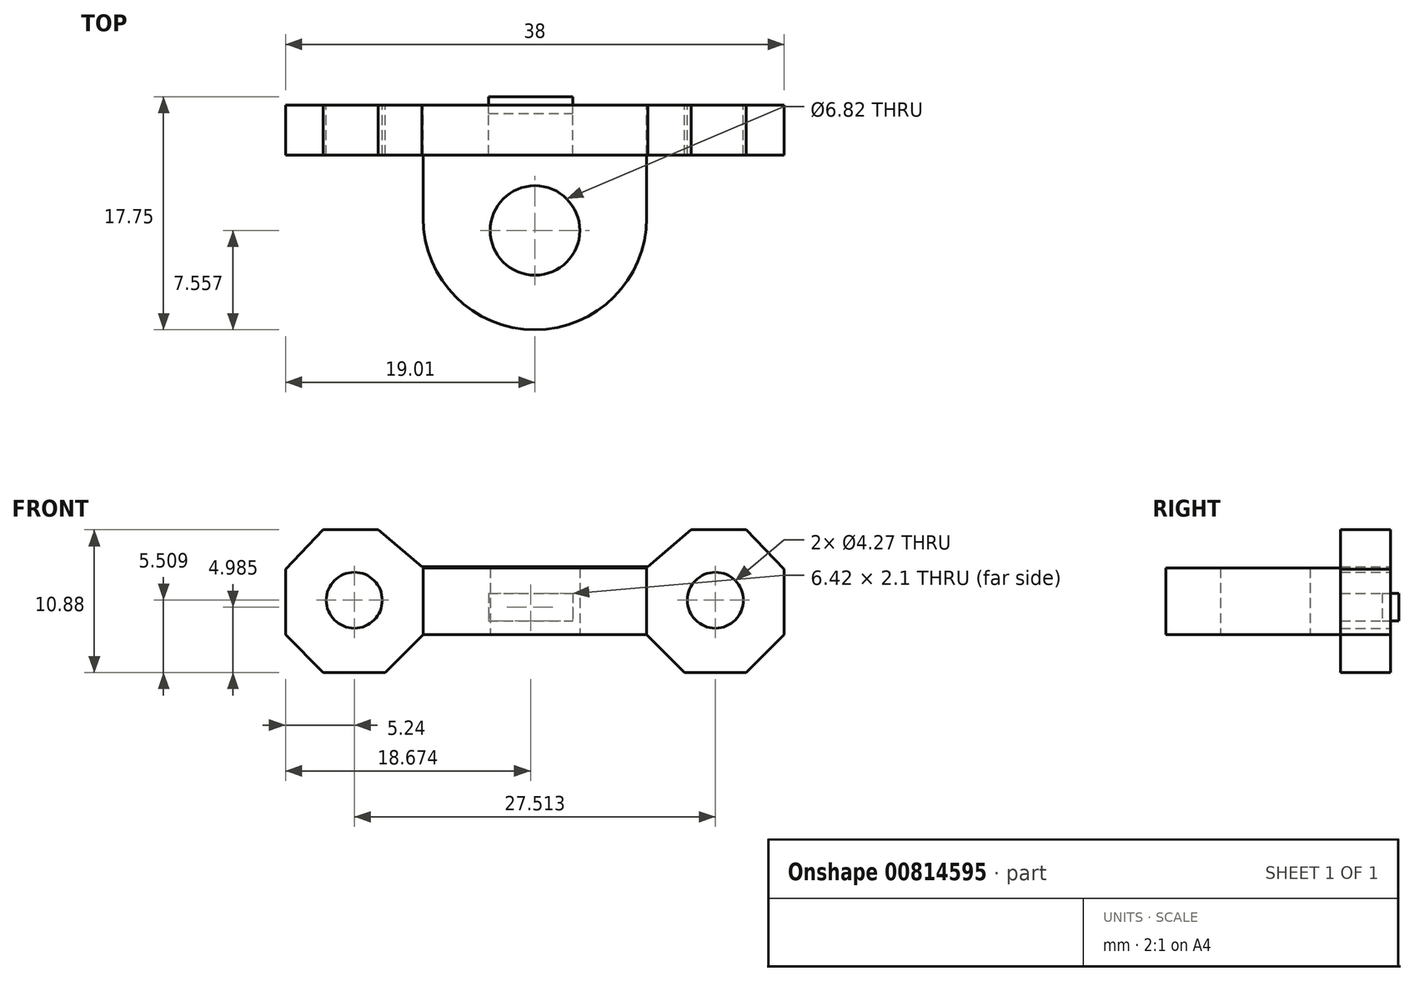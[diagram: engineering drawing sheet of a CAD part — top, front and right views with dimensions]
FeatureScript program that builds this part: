
annotation { "Feature Type Name" : "Feature", "Feature Type Description" : "" }
export const myFeature = defineFeature(function(context is Context, id is Id, definition is map)
    precondition{}
    {
        {
            var Q0;
            Q0=qCreatedBy(makeId("Front.planeOp"),FACE);
            var sketch = newSketch(context, id + "F0", { "sketchPlane" : qUnion([Q0])});
            skLineSegment(sketch, "E0", {"start": v(-50.5, 31.8) * mm, "end": v(-53.83, 34.6) * mm});
            skLineSegment(sketch, "E1", {"start": v(-53.83, 34.6) * mm, "end": v(-58.02, 34.6) * mm});
            skLineSegment(sketch, "E2", {"start": v(-58.02, 34.6) * mm, "end": v(-60.9, 31.59) * mm});
            skLineSegment(sketch, "E3", {"start": v(-60.9, 31.59) * mm, "end": v(-60.9, 26.6) * mm});
            skLineSegment(sketch, "E4", {"start": v(-60.9, 26.6) * mm, "end": v(-58.02, 23.72) * mm});
            skLineSegment(sketch, "E5", {"start": v(-58.02, 23.72) * mm, "end": v(-53.3, 23.72) * mm});
            skLineSegment(sketch, "E6", {"start": v(-53.3, 23.72) * mm, "end": v(-50.42, 26.6) * mm});
            skLineSegment(sketch, "E7", {"start": v(-50.42, 26.6) * mm, "end": v(-41.9, 26.6) * mm});
            skLineSegment(sketch, "E8", {"start": v(-50.5, 31.8) * mm, "end": v(-41.9, 31.8) * mm});
            skLineSegment(sketch, "E9", {"start": v(-41.9, 31.8) * mm, "end": v(-41.9, 26.6) * mm});
            skLineSegment(sketch, "E10.MirrorCS", {"start": v(-29.98, 34.6) * mm, "end": v(-25.79, 34.6) * mm});
            skLineSegment(sketch, "E11.MirrorCS", {"start": v(-33.3, 31.8) * mm, "end": v(-29.98, 34.6) * mm});
            skLineSegment(sketch, "E12.MirrorCS", {"start": v(-33.3, 31.8) * mm, "end": v(-41.9, 31.8) * mm});
            skLineSegment(sketch, "E13.MirrorCS", {"start": v(-33.39, 26.6) * mm, "end": v(-41.9, 26.6) * mm});
            skLineSegment(sketch, "E14.MirrorCS", {"start": v(-30.5, 23.72) * mm, "end": v(-33.39, 26.6) * mm});
            skLineSegment(sketch, "E15.MirrorCS", {"start": v(-25.79, 23.72) * mm, "end": v(-30.5, 23.72) * mm});
            skLineSegment(sketch, "E16.MirrorCS", {"start": v(-22.9, 26.6) * mm, "end": v(-25.79, 23.72) * mm});
            skLineSegment(sketch, "E17.MirrorCS", {"start": v(-22.9, 31.59) * mm, "end": v(-22.9, 26.6) * mm});
            skLineSegment(sketch, "E18.MirrorCS", {"start": v(-25.79, 34.6) * mm, "end": v(-22.9, 31.59) * mm});
            skCircle(sketch, "E19", {"center": v(-55.66, 29.23) * mm, "radius": 2.13 * mm});
            skCircle(sketch, "E20.MirrorC", {"center": v(-28.15, 29.23) * mm, "radius": 2.13 * mm});
            skLineSegment(sketch, "E21.bottom", {"start": v(-45.44, 29.75) * mm, "end": v(-39.01, 29.75) * mm});
            skLineSegment(sketch, "E21.top", {"start": v(-45.44, 27.66) * mm, "end": v(-39.01, 27.66) * mm});
            skLineSegment(sketch, "E21.left", {"start": v(-45.44, 29.75) * mm, "end": v(-45.44, 27.66) * mm});
            skLineSegment(sketch, "E21.right", {"start": v(-39.01, 29.75) * mm, "end": v(-39.01, 27.66) * mm});
            skSolve(sketch);
        }
        {
            var Q0;
            Q0 = qSketchRegion(id + "F0", true);
            extrude(context, id + "F1", {"entities" : qUnion([Q0]), "depth" : 3.8 * mm, "offsetDistance" : 25.4 * mm});
        }
        {
            var Q0;
            {var subQ5=sQuery(id+"F0.wireOp",EDGE,"E21.right");Q0=makeQuery(id+"F0.imprint","IMPRINT",FACE,{"disambiguationData":[TD([[makeQuery(id+"F0.imprint","IMPRINT",EDGE,{"derivedFrom":subQ5}),-1.0]])]});}
            var Q1;
            {var subQ5=sQuery(id+"F0.wireOp",EDGE,"E21.left");Q1=makeQuery(id+"F0.imprint","IMPRINT",FACE,{"disambiguationData":[TD([[makeQuery(id+"F0.imprint","IMPRINT",EDGE,{"derivedFrom":subQ5}),1.0]])]});}
            extrude(context, id + "F2", {"entities" : qUnion([Q0, Q1]), "endBound" : BoundingType.SYMMETRIC, "depth" : 1.27 * mm, "offsetDistance" : 25.4 * mm});
        }
        {
            var Q0;
            Q0=makeQuery(id+"F1.opExtrude","SWEPT_FACE",FACE,{"disambiguationData":[OSD([sQuery(id+"F0.wireOp",EDGE,"E7"),sQuery(id+"F0.wireOp",EDGE,"E13.MirrorCS")])]});
            var sketch = newSketch(context, id + "F3", { "sketchPlane" : qUnion([Q0])});
            skLineSegment(sketch, "E22", {"start": v(-50.42, 3.8) * mm, "end": v(-46.6, 3.81) * mm});
            skLineSegment(sketch, "E23", {"start": v(-36.63, 3.81) * mm, "end": v(-33.39, 3.81) * mm});
            skLineSegment(sketch, "E24", {"start": v(-50.42, 3.8) * mm, "end": v(-50.42, 8.6) * mm});
            skPoint(sketch, "E24.endSnap0", {"position": v(-41.61, 8.6) * mm});
            skLineSegment(sketch, "E25", {"start": v(-33.39, 3.81) * mm, "end": v(-33.39, 8.6) * mm});
            skArc(sketch, "E26", {"start": v(-33.39, 8.6) * mm, "mid": v(-41.9, 17.11) * mm, "end": v(-50.42, 8.6) * mm});
            skCircle(sketch, "E27", {"center": v(-41.9, 9.55) * mm, "radius": 3.41 * mm});
            skSolve(sketch);
        }
        {
            var Q0;
            {var subQ1=sQuery(id+"F3.wireOp",EDGE,"E22");Q0=makeQuery(id+"F3.imprint","IMPRINT",FACE,{"disambiguationData":[TD([[makeQuery(id+"F3.imprint","IMPRINT",EDGE,{"derivedFrom":subQ1}),1.0]])]});}
            extrude(context, id + "F4", {"entities" : qUnion([Q0]), "oppositeDirection" : true, "depth" : 5.08 * mm, "offsetDistance" : 25.4 * mm});
        }
    });
